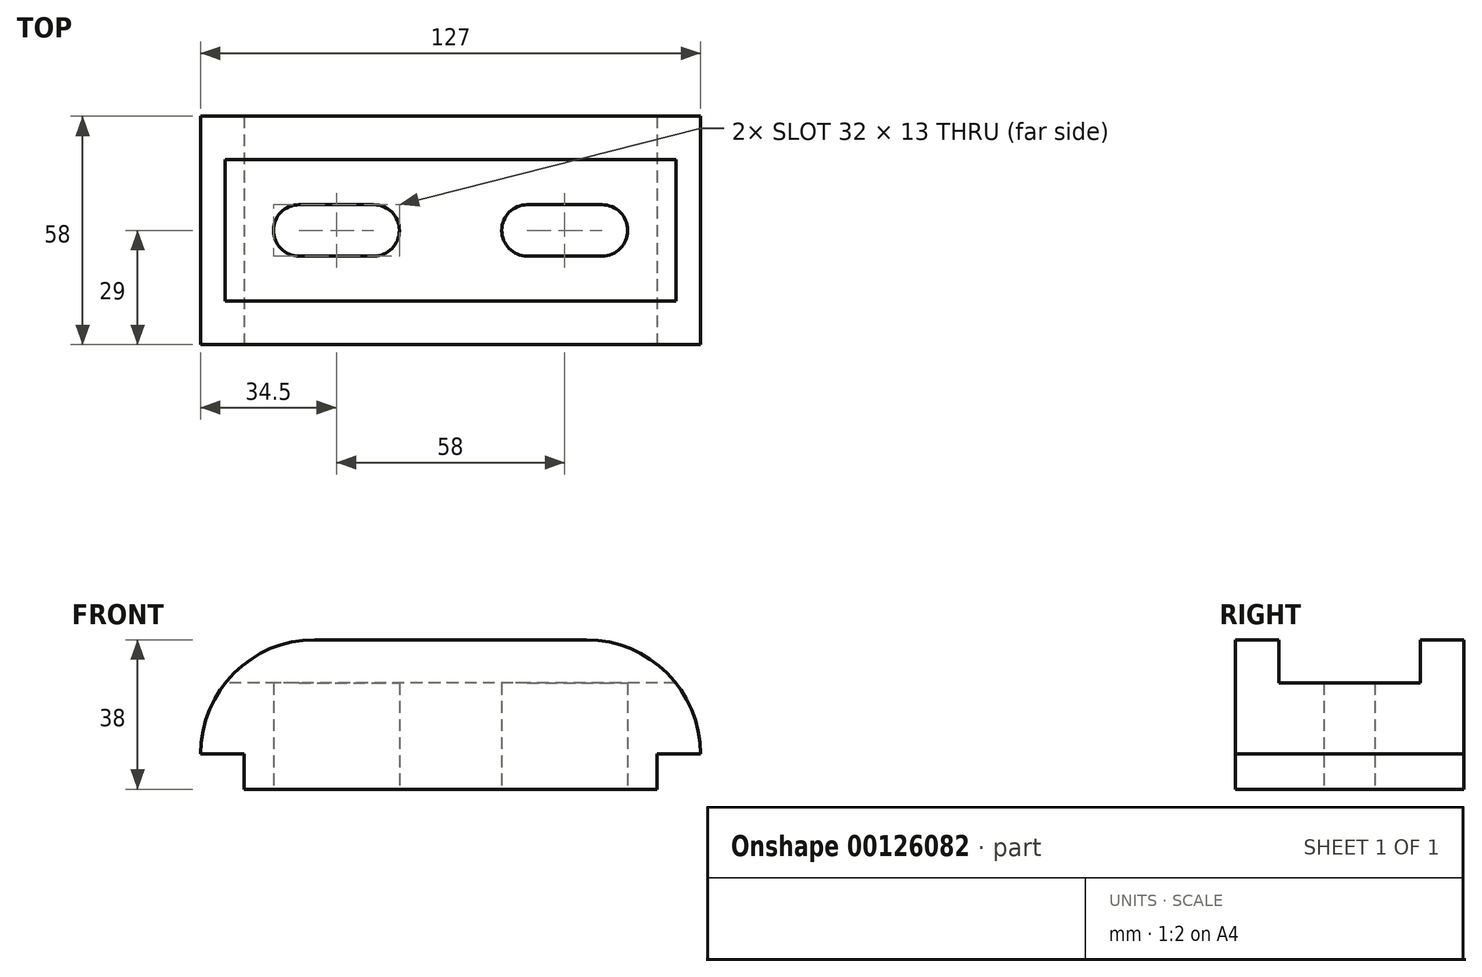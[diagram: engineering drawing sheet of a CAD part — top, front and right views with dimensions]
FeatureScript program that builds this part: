
annotation { "Feature Type Name" : "Feature", "Feature Type Description" : "" }
export const myFeature = defineFeature(function(context is Context, id is Id, definition is map)
    precondition{}
    {
        {
            var Q0;
            Q0=qCreatedBy(makeId("Front.planeOp"),FACE);
            var sketch = newSketch(context, id + "F0", { "sketchPlane" : qUnion([Q0])});
            skLineSegment(sketch, "E0", {"start": v(0, 0) * mm, "end": v(-52.5, 0) * mm});
            skLineSegment(sketch, "E1", {"start": v(0, 0) * mm, "end": v(52.5, 0) * mm});
            skLineSegment(sketch, "E2", {"start": v(-52.5, 0) * mm, "end": v(-52.5, 9) * mm});
            skLineSegment(sketch, "E3", {"start": v(-52.5, 9) * mm, "end": v(-63.5, 9) * mm});
            skLineSegment(sketch, "E4", {"start": v(52.5, 0) * mm, "end": v(52.5, 9) * mm});
            skLineSegment(sketch, "E5", {"start": v(52.5, 9) * mm, "end": v(63.5, 9) * mm});
            skLineSegment(sketch, "E6", {"start": v(-63.5, 9) * mm, "end": v(-63.5, 38) * mm});
            skLineSegment(sketch, "E7", {"start": v(63.5, 9) * mm, "end": v(63.5, 38) * mm});
            skLineSegment(sketch, "E8", {"start": v(63.5, 38) * mm, "end": v(-63.5, 38) * mm});
            skSolve(sketch);
        }
        {
            var Q0;
            Q0 = qSketchRegion(id + "F0", true);
            extrude(context, id + "F1", {"entities" : qUnion([Q0]), "endBound" : BoundingType.SYMMETRIC, "oppositeDirection" : true, "depth" : 58 * mm});
        }
        {
            var Q0;
            Q0=makeQuery(id+"F1.opExtrude","SWEPT_EDGE",EDGE,{"disambiguationData":[OSD([sQuery(id+"F0.wireOp",EDGE,"E7"),sQuery(id+"F0.wireOp",EDGE,"E8")])]});
            var Q1;
            Q1=makeQuery(id+"F1.opExtrude","SWEPT_EDGE",EDGE,{"disambiguationData":[OSD([sQuery(id+"F0.wireOp",EDGE,"E6"),sQuery(id+"F0.wireOp",EDGE,"E8")])]});
            fillet(context, id + "F2", {"entities" : qUnion([Q0, Q1]), "radius" : 29 * mm, "tangentPropagation" : true, "allowEdgeOverflow" : false});
        }
        {
            var Q0;
            Q0=qCreatedBy(makeId("Top.planeOp"),FACE);
            var sketch = newSketch(context, id + "F3", { "sketchPlane" : qUnion([Q0])});
            skLineSegment(sketch, "E9", {"start": v(0, 0) * mm, "end": v(-19.5, 0) * mm, "construction": true});
            skLineSegment(sketch, "E10", {"start": v(-19.5, 0) * mm, "end": v(-38.5, 0) * mm, "construction": true});
            skLineSegment(sketch, "E11", {"start": v(0, 0) * mm, "end": v(19.5, 0) * mm, "construction": true});
            skLineSegment(sketch, "E12", {"start": v(19.5, 0) * mm, "end": v(38.5, 0) * mm, "construction": true});
            skArc(sketch, "E13", {"start": v(-38.5, 6.5) * mm, "mid": v(-45, 0) * mm, "end": v(-38.5, -6.5) * mm});
            skArc(sketch, "E14", {"start": v(-19.5, -6.5) * mm, "mid": v(-13, 0) * mm, "end": v(-19.5, 6.5) * mm});
            skArc(sketch, "E15", {"start": v(19.5, 6.5) * mm, "mid": v(13, 0) * mm, "end": v(19.5, -6.5) * mm});
            skArc(sketch, "E16", {"start": v(38.5, -6.5) * mm, "mid": v(45, 0) * mm, "end": v(38.5, 6.5) * mm});
            skLineSegment(sketch, "E17", {"start": v(-38.5, -6.5) * mm, "end": v(-19.5, -6.5) * mm});
            skLineSegment(sketch, "E18", {"start": v(-38.5, 6.5) * mm, "end": v(-19.5, 6.5) * mm});
            skLineSegment(sketch, "E19", {"start": v(19.5, -6.5) * mm, "end": v(38.5, -6.5) * mm});
            skLineSegment(sketch, "E20", {"start": v(19.5, 6.5) * mm, "end": v(38.5, 6.5) * mm});
            skSolve(sketch);
        }
        {
            var Q0;
            Q0=makeQuery(id+"F3.imprint","IMPRINT",FACE,{"disambiguationData":[TD([[makeQuery(id+"F3.imprint","IMPRINT",EDGE,{"derivedFrom":sQuery(id+"F3.wireOp",EDGE,"E13")}),1.0]])]});
            var Q1;
            Q1=makeQuery(id+"F3.imprint","IMPRINT",FACE,{"disambiguationData":[TD([[makeQuery(id+"F3.imprint","IMPRINT",EDGE,{"derivedFrom":sQuery(id+"F3.wireOp",EDGE,"E15")}),1.0]])]});
            var Q2;
            Q2=makeQuery(id+"F1.opExtrude","SWEPT_FACE",FACE,{"disambiguationData":[OSD([sQuery(id+"F0.wireOp",EDGE,"E8")])]});
            extrude(context, id + "F4", {"entities" : qUnion([Q0, Q1]), "operationType" : NewBodyOperationType.REMOVE, "endBound" : BoundingType.UP_TO_SURFACE, "endBoundEntityFace" : qUnion([Q2]), "depth" : 25 * mm});
        }
        {
            var Q0;
            Q0=qCreatedBy(makeId("Front.planeOp"),FACE);
            var sketch = newSketch(context, id + "F5", { "sketchPlane" : qUnion([Q0])});
            skLineSegment(sketch, "E21", {"start": v(0, 0) * mm, "end": v(0, 38) * mm, "construction": true});
            skLineSegment(sketch, "E22", {"start": v(0, 38) * mm, "end": v(63.5, 38) * mm});
            skLineSegment(sketch, "E23", {"start": v(0, 38) * mm, "end": v(-63.5, 38) * mm});
            skLineSegment(sketch, "E24", {"start": v(-63.5, 38) * mm, "end": v(-63.5, 27) * mm});
            skLineSegment(sketch, "E25", {"start": v(63.5, 38) * mm, "end": v(63.5, 27) * mm});
            skLineSegment(sketch, "E26", {"start": v(63.5, 27) * mm, "end": v(-63.5, 27) * mm});
            skSolve(sketch);
        }
        {
            var Q0;
            Q0 = qSketchRegion(id + "F5", true);
            extrude(context, id + "F6", {"entities" : qUnion([Q0]), "operationType" : NewBodyOperationType.REMOVE, "endBound" : BoundingType.SYMMETRIC, "oppositeDirection" : true, "depth" : 36 * mm});
        }
    });
